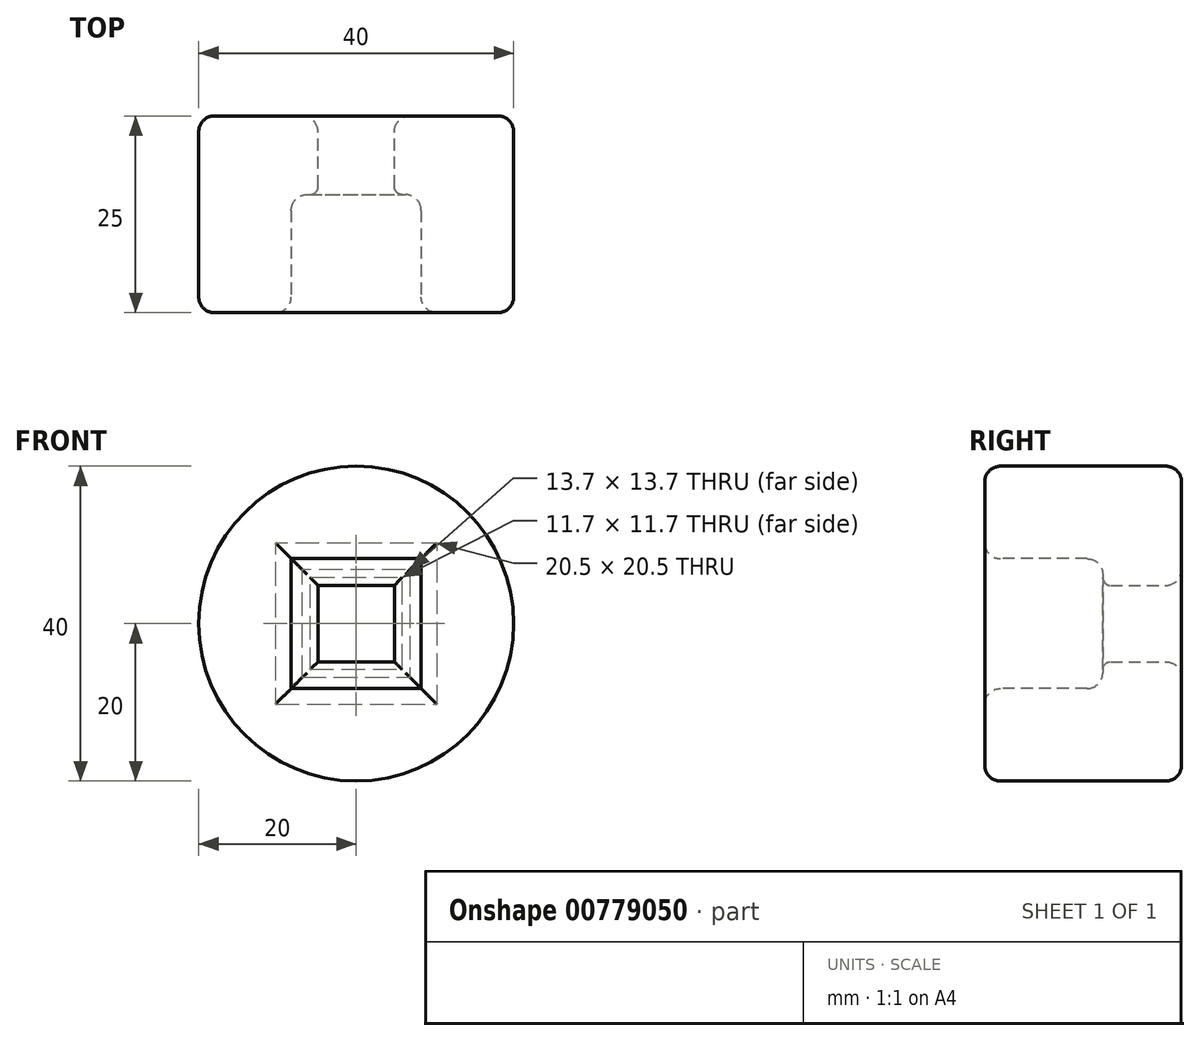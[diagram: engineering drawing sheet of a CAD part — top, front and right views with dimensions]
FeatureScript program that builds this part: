
annotation { "Feature Type Name" : "Feature", "Feature Type Description" : "" }
export const myFeature = defineFeature(function(context is Context, id is Id, definition is map)
    precondition{}
    {
        {
            var Q0;
            Q0=qCreatedBy(makeId("Front.planeOp"),FACE);
            var sketch = newSketch(context, id + "F0", { "sketchPlane" : qUnion([Q0])});
            skCircle(sketch, "E0", {"center": v(0, 0) * mm, "radius": 20 * mm});
            skSolve(sketch);
        }
        {
            var Q0;
            Q0=makeQuery(id+"F0.imprint","IMPRINT",FACE,{"disambiguationData":[TD([[makeQuery(id+"F0.imprint","IMPRINT",EDGE,{"derivedFrom":sQuery(id+"F0.wireOp",EDGE,"E0")}),1.0]])]});
            extrude(context, id + "F1", {"entities" : qUnion([Q0]), "depth" : 25 * mm, "offsetDistance" : 25 * mm});
        }
        {
            var Q0;
            Q0=makeQuery(id+"F1.opExtrude","CAP_FACE",FACE,{"disambiguationData":[OSD([sQuery(id+"F0.wireOp",EDGE,"E0")])],"isStart":false});
            var sketch = newSketch(context, id + "F2", { "sketchPlane" : qUnion([Q0])});
            skLineSegment(sketch, "E1.bottom", {"start": v(-8.25, 8.25) * mm, "end": v(8.25, 8.25) * mm});
            skLineSegment(sketch, "E1.top", {"start": v(-8.25, -8.25) * mm, "end": v(8.25, -8.25) * mm});
            skLineSegment(sketch, "E1.left", {"start": v(-8.25, 8.25) * mm, "end": v(-8.25, -8.25) * mm});
            skLineSegment(sketch, "E1.right", {"start": v(8.25, 8.25) * mm, "end": v(8.25, -8.25) * mm});
            skSolve(sketch);
        }
        {
            var Q0;
            Q0 = qSketchRegion(id + "F2", true);
            extrude(context, id + "F3", {"entities" : qUnion([Q0]), "operationType" : NewBodyOperationType.REMOVE, "oppositeDirection" : true, "depth" : 15 * mm, "offsetDistance" : 25 * mm});
        }
        {
            var Q0;
            Q0=makeQuery(id+"F1.opExtrude","CAP_FACE",FACE,{"disambiguationData":[OSD([sQuery(id+"F0.wireOp",EDGE,"E0")])],"isStart":true});
            var sketch = newSketch(context, id + "F4", { "sketchPlane" : qUnion([Q0])});
            skLineSegment(sketch, "E2.bottom", {"start": v(-4.85, 4.85) * mm, "end": v(4.85, 4.85) * mm});
            skLineSegment(sketch, "E2.top", {"start": v(-4.85, -4.85) * mm, "end": v(4.85, -4.85) * mm});
            skLineSegment(sketch, "E2.left", {"start": v(-4.85, 4.85) * mm, "end": v(-4.85, -4.85) * mm});
            skLineSegment(sketch, "E2.right", {"start": v(4.85, 4.85) * mm, "end": v(4.85, -4.85) * mm});
            skSolve(sketch);
        }
        {
            var Q0;
            Q0 = qSketchRegion(id + "F4", true);
            extrude(context, id + "F5", {"entities" : qUnion([Q0]), "operationType" : NewBodyOperationType.REMOVE, "oppositeDirection" : true, "depth" : 25 * mm, "offsetDistance" : 25 * mm});
        }
        {
            var Q0;
            Q0=makeQuery(id+"F3.boolean.opBoolean","COPY",EDGE,{"derivedFrom":makeQuery(id+"F3.opExtrude","CAP_EDGE",EDGE,{"disambiguationData":[OSD([sQuery(id+"F2.wireOp",EDGE,"E1.top")])],"isStart":false})});
            var Q1;
            Q1=makeQuery(id+"F3.boolean.opBoolean","COPY",EDGE,{"derivedFrom":makeQuery(id+"F3.opExtrude","CAP_EDGE",EDGE,{"disambiguationData":[OSD([sQuery(id+"F2.wireOp",EDGE,"E1.left")])],"isStart":false})});
            var Q2;
            Q2=makeQuery(id+"F3.boolean.opBoolean","COPY",EDGE,{"derivedFrom":makeQuery(id+"F3.opExtrude","CAP_EDGE",EDGE,{"disambiguationData":[OSD([sQuery(id+"F2.wireOp",EDGE,"E1.right")])],"isStart":false})});
            var Q3;
            Q3=makeQuery(id+"F3.boolean.opBoolean","COPY",EDGE,{"derivedFrom":makeQuery(id+"F3.opExtrude","CAP_EDGE",EDGE,{"disambiguationData":[OSD([sQuery(id+"F2.wireOp",EDGE,"E1.bottom")])],"isStart":false})});
            var Q4;
            Q4=makeQuery(id+"F1.opExtrude","CAP_FACE",FACE,{"disambiguationData":[OSD([sQuery(id+"F0.wireOp",EDGE,"E0")])],"isStart":false});
            var Q5;
            Q5=makeQuery(id+"F1.opExtrude","CAP_FACE",FACE,{"disambiguationData":[OSD([sQuery(id+"F0.wireOp",EDGE,"E0")])],"isStart":true});
            fillet(context, id + "F6", {"entities" : qUnion([Q0, Q1, Q2, Q3, Q4, Q5]), "radius" : 2 * mm, "tangentPropagation" : true, "allowEdgeOverflow" : false});
        }
        {
            var Q0;
            Q0=makeQuery(id+"F5.boolean.opBoolean","INTERSECT",EDGE,{"derivedFrom":[makeQuery(id+"F3.boolean.opBoolean","COPY",FACE,{"derivedFrom":makeQuery(id+"F3.opExtrude","CAP_FACE",FACE,{"disambiguationData":[OSD([sQuery(id+"F2.wireOp",EDGE,"E1.bottom"),sQuery(id+"F2.wireOp",EDGE,"E1.top"),sQuery(id+"F2.wireOp",EDGE,"E1.left"),sQuery(id+"F2.wireOp",EDGE,"E1.right")])],"isStart":false})}),makeQuery(id+"F5.opExtrude","SWEPT_FACE",FACE,{"disambiguationData":[OSD([sQuery(id+"F4.wireOp",EDGE,"E2.top")])]})]});
            var Q1;
            Q1=makeQuery(id+"F5.boolean.opBoolean","INTERSECT",EDGE,{"derivedFrom":[makeQuery(id+"F3.boolean.opBoolean","COPY",FACE,{"derivedFrom":makeQuery(id+"F3.opExtrude","CAP_FACE",FACE,{"disambiguationData":[OSD([sQuery(id+"F2.wireOp",EDGE,"E1.bottom"),sQuery(id+"F2.wireOp",EDGE,"E1.top"),sQuery(id+"F2.wireOp",EDGE,"E1.left"),sQuery(id+"F2.wireOp",EDGE,"E1.right")])],"isStart":false})}),makeQuery(id+"F5.opExtrude","SWEPT_FACE",FACE,{"disambiguationData":[OSD([sQuery(id+"F4.wireOp",EDGE,"E2.right")])]})]});
            var Q2;
            Q2=makeQuery(id+"F5.boolean.opBoolean","INTERSECT",EDGE,{"derivedFrom":[makeQuery(id+"F3.boolean.opBoolean","COPY",FACE,{"derivedFrom":makeQuery(id+"F3.opExtrude","CAP_FACE",FACE,{"disambiguationData":[OSD([sQuery(id+"F2.wireOp",EDGE,"E1.bottom"),sQuery(id+"F2.wireOp",EDGE,"E1.top"),sQuery(id+"F2.wireOp",EDGE,"E1.left"),sQuery(id+"F2.wireOp",EDGE,"E1.right")])],"isStart":false})}),makeQuery(id+"F5.opExtrude","SWEPT_FACE",FACE,{"disambiguationData":[OSD([sQuery(id+"F4.wireOp",EDGE,"E2.bottom")])]})]});
            var Q3;
            Q3=makeQuery(id+"F5.boolean.opBoolean","INTERSECT",EDGE,{"derivedFrom":[makeQuery(id+"F3.boolean.opBoolean","COPY",FACE,{"derivedFrom":makeQuery(id+"F3.opExtrude","CAP_FACE",FACE,{"disambiguationData":[OSD([sQuery(id+"F2.wireOp",EDGE,"E1.bottom"),sQuery(id+"F2.wireOp",EDGE,"E1.top"),sQuery(id+"F2.wireOp",EDGE,"E1.left"),sQuery(id+"F2.wireOp",EDGE,"E1.right")])],"isStart":false})}),makeQuery(id+"F5.opExtrude","SWEPT_FACE",FACE,{"disambiguationData":[OSD([sQuery(id+"F4.wireOp",EDGE,"E2.left")])]})]});
            fillet(context, id + "F7", {"entities" : qUnion([Q0, Q1, Q2, Q3]), "radius" : 1 * mm, "tangentPropagation" : true, "allowEdgeOverflow" : false});
        }
    });
